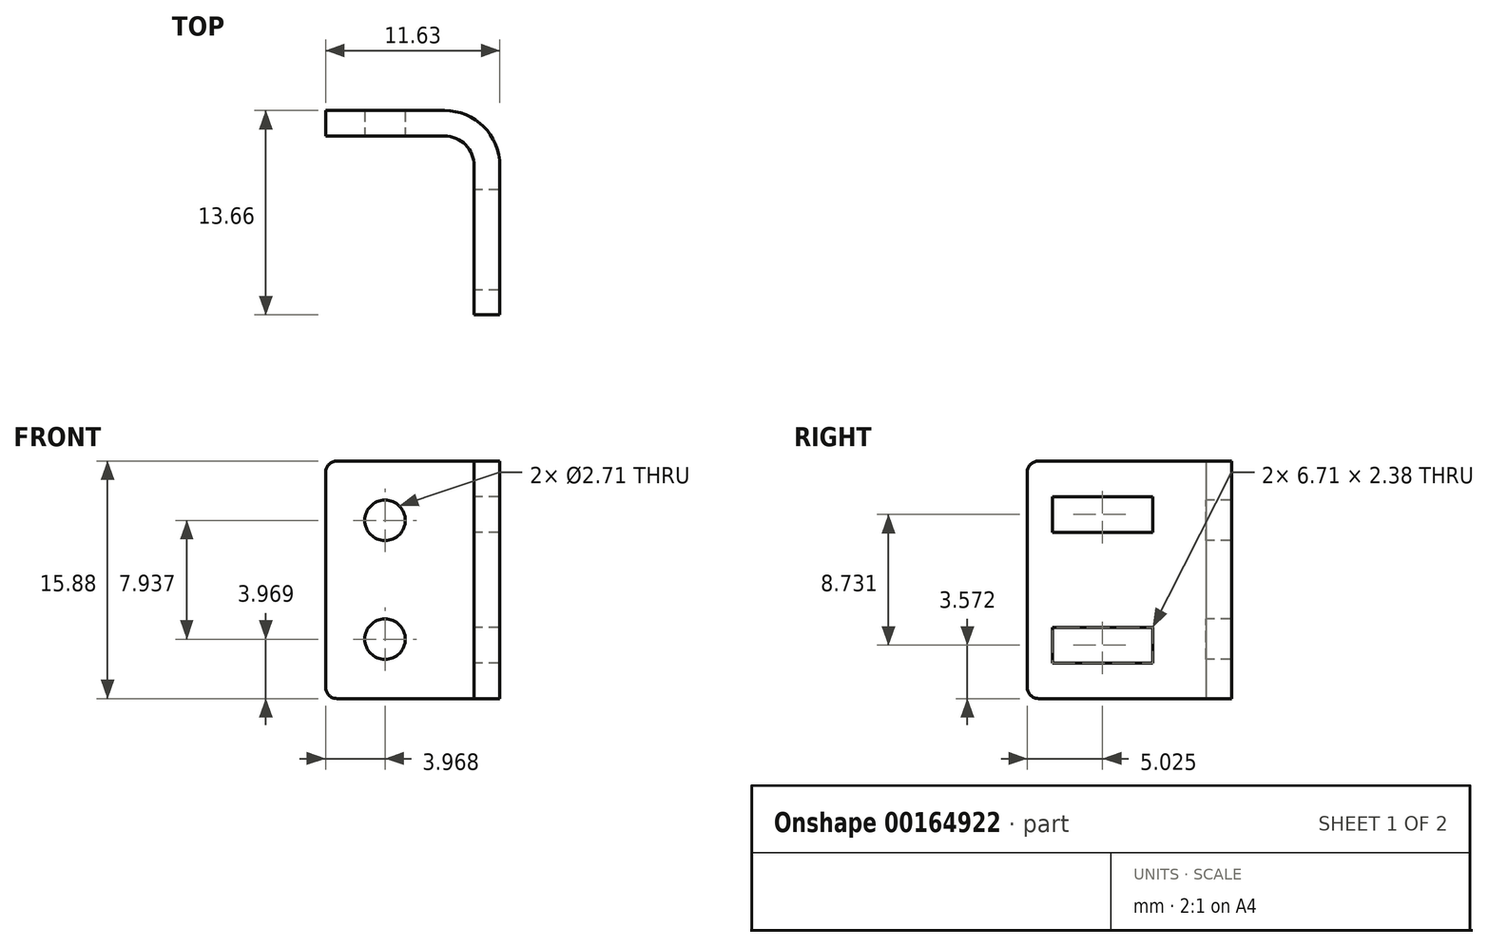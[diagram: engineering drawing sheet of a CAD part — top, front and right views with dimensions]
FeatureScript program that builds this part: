
annotation { "Feature Type Name" : "Feature", "Feature Type Description" : "" }
export const myFeature = defineFeature(function(context is Context, id is Id, definition is map)
    precondition{}
    {
        {
            var Q0;
            Q0=qCreatedBy(makeId("Top.planeOp"),FACE);
            var sketch = newSketch(context, id + "F0", { "sketchPlane" : qUnion([Q0])});
            skLineSegment(sketch, "E0.top", {"start": v(0, -11.95) * mm, "end": v(1.7, -11.95) * mm});
            skLineSegment(sketch, "E0.left", {"start": v(0, 0) * mm, "end": v(0, -11.95) * mm});
            skLineSegment(sketch, "E0.right", {"start": v(1.7, 1.7) * mm, "end": v(1.7, -11.95) * mm});
            skLineSegment(sketch, "E1.bottom", {"start": v(0, 0) * mm, "end": v(-9.92, 0) * mm});
            skLineSegment(sketch, "E1.top", {"start": v(1.7, 1.7) * mm, "end": v(-9.92, 1.7) * mm});
            skLineSegment(sketch, "E1.right", {"start": v(-9.92, 0) * mm, "end": v(-9.92, 1.7) * mm});
            skSolve(sketch);
        }
        {
            var Q0;
            Q0 = qSketchRegion(id + "F0", true);
            extrude(context, id + "F1", {"entities" : qUnion([Q0]), "depth" : 15.88 * mm});
        }
        {
            var Q0;
            Q0=makeQuery(id+"F1.opExtrude","CAP_EDGE",EDGE,{"disambiguationData":[OSD([sQuery(id+"F0.wireOp",EDGE,"E1.right")])],"isStart":false});
            var Q1;
            Q1=makeQuery(id+"F1.opExtrude","CAP_EDGE",EDGE,{"disambiguationData":[OSD([sQuery(id+"F0.wireOp",EDGE,"E1.right")])],"isStart":true});
            var Q2;
            Q2=makeQuery(id+"F1.opExtrude","CAP_EDGE",EDGE,{"disambiguationData":[OSD([sQuery(id+"F0.wireOp",EDGE,"E0.top")])],"isStart":true});
            var Q3;
            Q3=makeQuery(id+"F1.opExtrude","CAP_EDGE",EDGE,{"disambiguationData":[OSD([sQuery(id+"F0.wireOp",EDGE,"E0.top")])],"isStart":false});
            fillet(context, id + "F2", {"entities" : qUnion([Q0, Q1, Q2, Q3]), "radius" : 0.76 * mm, "tangentPropagation" : true, "allowEdgeOverflow" : false});
        }
        {
            var Q0;
            Q0=makeQuery(id+"F1.opExtrude","SWEPT_EDGE",EDGE,{"disambiguationData":[OSD([sQuery(id+"F0.wireOp",EDGE,"E0.left"),sQuery(id+"F0.wireOp",EDGE,"E1.bottom")])]});
            fillet(context, id + "F3", {"entities" : qUnion([Q0]), "radius" : 1.98 * mm, "tangentPropagation" : true, "allowEdgeOverflow" : false});
        }
        {
            var Q0;
            Q0=makeQuery(id+"F1.opExtrude","SWEPT_EDGE",EDGE,{"disambiguationData":[OSD([sQuery(id+"F0.wireOp",EDGE,"E0.right"),sQuery(id+"F0.wireOp",EDGE,"E1.top")])]});
            fillet(context, id + "F4", {"entities" : qUnion([Q0]), "radius" : 3.7 * mm, "tangentPropagation" : true, "allowEdgeOverflow" : false});
        }
        {
            var Q0;
            Q0=makeQuery(id+"F1.opExtrude","SWEPT_FACE",FACE,{"disambiguationData":[OSD([sQuery(id+"F0.wireOp",EDGE,"E0.left")])]});
            var sketch = newSketch(context, id + "F5", { "sketchPlane" : qUnion([Q0])});
            skLineSegment(sketch, "E2.bottom", {"start": v(1.98, 15.88) * mm, "end": v(3.57, 15.88) * mm, "construction": true});
            skLineSegment(sketch, "E2.top", {"start": v(1.98, 13.5) * mm, "end": v(3.57, 13.5) * mm, "construction": true});
            skLineSegment(sketch, "E2.left", {"start": v(1.98, 15.88) * mm, "end": v(1.98, 13.5) * mm, "construction": true});
            skLineSegment(sketch, "E2.right", {"start": v(3.57, 15.88) * mm, "end": v(3.57, 13.5) * mm, "construction": true});
            skLineSegment(sketch, "E3.bottom", {"start": v(1.98, 0) * mm, "end": v(3.57, 0) * mm, "construction": true});
            skLineSegment(sketch, "E3.top", {"start": v(1.98, 2.38) * mm, "end": v(3.57, 2.38) * mm, "construction": true});
            skLineSegment(sketch, "E3.left", {"start": v(1.98, 0) * mm, "end": v(1.98, 2.38) * mm, "construction": true});
            skLineSegment(sketch, "E3.right", {"start": v(3.57, 0) * mm, "end": v(3.57, 2.38) * mm, "construction": true});
            skLineSegment(sketch, "E4.bottom", {"start": v(3.57, 13.5) * mm, "end": v(10.28, 13.5) * mm});
            skLineSegment(sketch, "E4.top", {"start": v(3.57, 11.11) * mm, "end": v(10.28, 11.11) * mm});
            skLineSegment(sketch, "E4.left", {"start": v(3.57, 13.5) * mm, "end": v(3.57, 11.11) * mm});
            skLineSegment(sketch, "E4.right", {"start": v(10.28, 13.5) * mm, "end": v(10.28, 11.11) * mm});
            skLineSegment(sketch, "E5.bottom", {"start": v(3.57, 2.38) * mm, "end": v(10.28, 2.38) * mm});
            skLineSegment(sketch, "E5.top", {"start": v(3.57, 4.76) * mm, "end": v(10.28, 4.76) * mm});
            skLineSegment(sketch, "E5.left", {"start": v(3.57, 2.38) * mm, "end": v(3.57, 4.76) * mm});
            skLineSegment(sketch, "E5.right", {"start": v(10.28, 2.38) * mm, "end": v(10.28, 4.76) * mm});
            skSolve(sketch);
        }
        {
            var Q0;
            Q0 = qSketchRegion(id + "F5", true);
            var Q1;
            Q1=makeQuery(id+"F1.opExtrude","SWEPT_FACE",FACE,{"disambiguationData":[OSD([sQuery(id+"F0.wireOp",EDGE,"E0.right")])]});
            extrude(context, id + "F6", {"entities" : qUnion([Q0]), "operationType" : NewBodyOperationType.REMOVE, "endBound" : BoundingType.UP_TO_SURFACE, "oppositeDirection" : true, "endBoundEntityFace" : qUnion([Q1]), "depth" : 25.4 * mm});
        }
        {
            var Q0;
            Q0=makeQuery(id+"F1.opExtrude","SWEPT_FACE",FACE,{"disambiguationData":[OSD([sQuery(id+"F0.wireOp",EDGE,"E1.bottom")])]});
            var sketch = newSketch(context, id + "F7", { "sketchPlane" : qUnion([Q0])});
            skLineSegment(sketch, "E6.bottom", {"start": v(-1.98, 15.88) * mm, "end": v(-5.95, 15.88) * mm, "construction": true});
            skLineSegment(sketch, "E6.top", {"start": v(-1.98, 11.9) * mm, "end": v(-5.95, 11.9) * mm, "construction": true});
            skLineSegment(sketch, "E6.left", {"start": v(-1.98, 15.88) * mm, "end": v(-1.98, 11.9) * mm, "construction": true});
            skLineSegment(sketch, "E6.right", {"start": v(-5.95, 15.88) * mm, "end": v(-5.95, 11.9) * mm, "construction": true});
            skLineSegment(sketch, "E7.bottom", {"start": v(-1.98, 0) * mm, "end": v(-5.95, 0) * mm, "construction": true});
            skLineSegment(sketch, "E7.top", {"start": v(-1.98, 3.97) * mm, "end": v(-5.95, 3.97) * mm, "construction": true});
            skLineSegment(sketch, "E7.left", {"start": v(-1.98, 0) * mm, "end": v(-1.98, 3.97) * mm, "construction": true});
            skLineSegment(sketch, "E7.right", {"start": v(-5.95, 0) * mm, "end": v(-5.95, 3.97) * mm, "construction": true});
            skCircle(sketch, "E8", {"center": v(-5.95, 11.9) * mm, "radius": 1.35 * mm});
            skCircle(sketch, "E9", {"center": v(-5.95, 3.97) * mm, "radius": 1.35 * mm});
            skSolve(sketch);
        }
        {
            var Q0;
            Q0 = qSketchRegion(id + "F7", true);
            var Q1;
            Q1=makeQuery(id+"F1.opExtrude","SWEPT_FACE",FACE,{"disambiguationData":[OSD([sQuery(id+"F0.wireOp",EDGE,"E1.top")])]});
            extrude(context, id + "F8", {"entities" : qUnion([Q0]), "operationType" : NewBodyOperationType.REMOVE, "endBound" : BoundingType.UP_TO_SURFACE, "oppositeDirection" : true, "endBoundEntityFace" : qUnion([Q1]), "depth" : 25.4 * mm});
        }
    });
